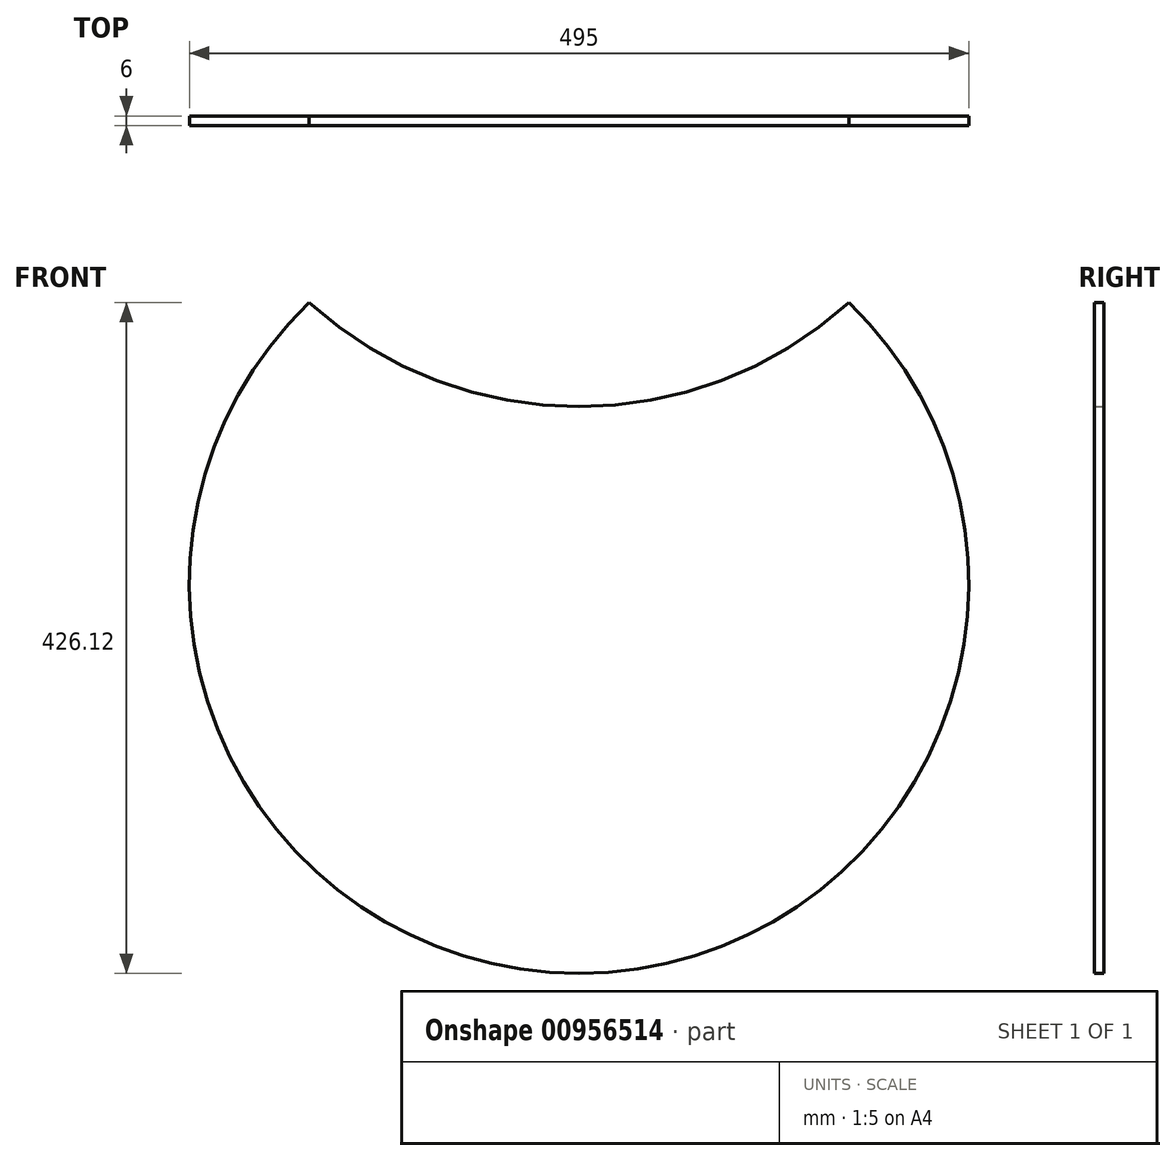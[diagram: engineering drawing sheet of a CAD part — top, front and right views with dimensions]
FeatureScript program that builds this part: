
annotation { "Feature Type Name" : "Feature", "Feature Type Description" : "" }
export const myFeature = defineFeature(function(context is Context, id is Id, definition is map)
    precondition{}
    {
        {
            var Q0;
            Q0=qCreatedBy(makeId("Front.planeOp"),FACE);
            var sketch = newSketch(context, id + "F0", { "sketchPlane" : qUnion([Q0])});
            skCircle(sketch, "E0", {"center": v(0, 0) * mm, "radius": 247.5 * mm});
            skArc(sketch, "E1", {"start": v(-171.32, 178.62) * mm, "mid": v(0, 112.5) * mm, "end": v(171.32, 178.62) * mm});
            skSolve(sketch);
        }
        {
            var Q0;
            {var subQ0=sQuery(id+"F0.wireOp",EDGE,"E1");Q0=makeQuery(id+"F0.imprint","IMPRINT",FACE,{"disambiguationData":[TD([[makeQuery(id+"F0.imprint","IMPRINT",EDGE,{"derivedFrom":subQ0}),-1.0]])]});}
            extrude(context, id + "F1", {"entities" : qUnion([Q0]), "depth" : 6 * mm, "offsetDistance" : 25.4 * mm});
        }
    });
